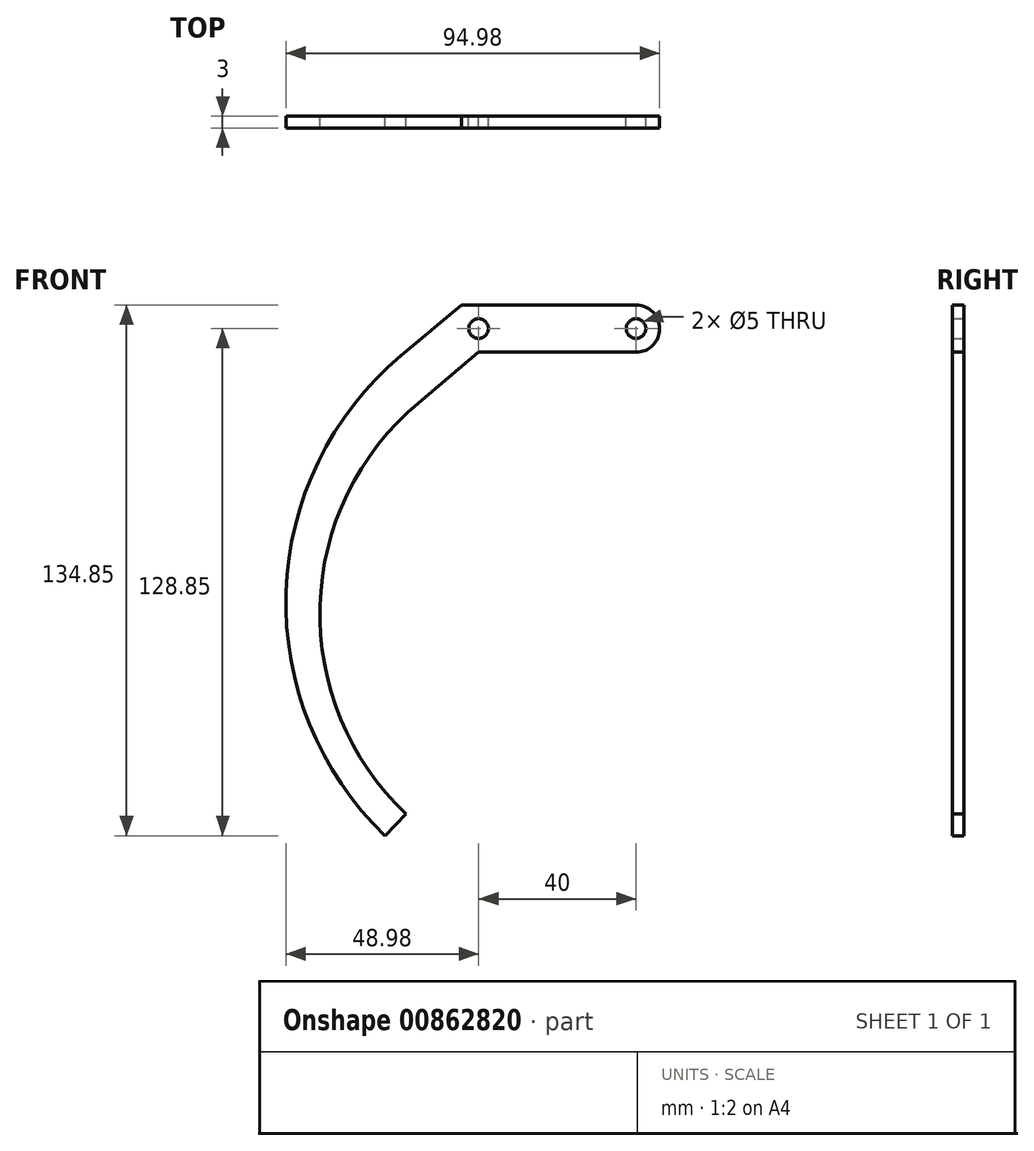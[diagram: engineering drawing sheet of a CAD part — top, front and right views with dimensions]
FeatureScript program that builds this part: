
annotation { "Feature Type Name" : "Feature", "Feature Type Description" : "" }
export const myFeature = defineFeature(function(context is Context, id is Id, definition is map)
    precondition{}
    {
        {
            var Q0;
            Q0=qCreatedBy(makeId("Front.planeOp"),FACE);
            var sketch = newSketch(context, id + "F0", { "sketchPlane" : qUnion([Q0])});
            skArc(sketch, "E0", {"start": v(0, -6) * mm, "mid": v(6, 0) * mm, "end": v(0, 6) * mm});
            skLineSegment(sketch, "E1", {"start": v(0, 6) * mm, "end": v(-44.37, 6) * mm});
            skLineSegment(sketch, "E2", {"start": v(0, -6) * mm, "end": v(-40, -6) * mm});
            skCircle(sketch, "E3", {"center": v(-40, 0) * mm, "radius": 2.5 * mm});
            skLineSegment(sketch, "E4", {"start": v(-40, -6) * mm, "end": v(-55.32, -18.86) * mm});
            skLineSegment(sketch, "E5", {"start": v(-44.37, 6) * mm, "end": v(-59.69, -6.86) * mm});
            skArc(sketch, "E6", {"start": v(-55.32, -18.86) * mm, "mid": v(-80.3, -70.36) * mm, "end": v(-58.48, -123.28) * mm});
            skArc(sketch, "E7", {"start": v(-59.69, -6.86) * mm, "mid": v(-88.93, -66.95) * mm, "end": v(-63.74, -128.85) * mm});
            skLineSegment(sketch, "E8", {"start": v(-58.48, -123.28) * mm, "end": v(-63.74, -128.85) * mm});
            skCircle(sketch, "E9", {"center": v(0, 0) * mm, "radius": 2.5 * mm});
            skSolve(sketch);
        }
        {
            var Q0;
            Q0=makeQuery(id+"F0.imprint","IMPRINT",FACE,{"disambiguationData":[TD([[makeQuery(id+"F0.imprint","IMPRINT",EDGE,{"derivedFrom":sQuery(id+"F0.wireOp",EDGE,"E0")}),1.0]])]});
            extrude(context, id + "F1", {"entities" : qUnion([Q0]), "depth" : 3 * mm, "offsetDistance" : 25 * mm});
        }
    });
